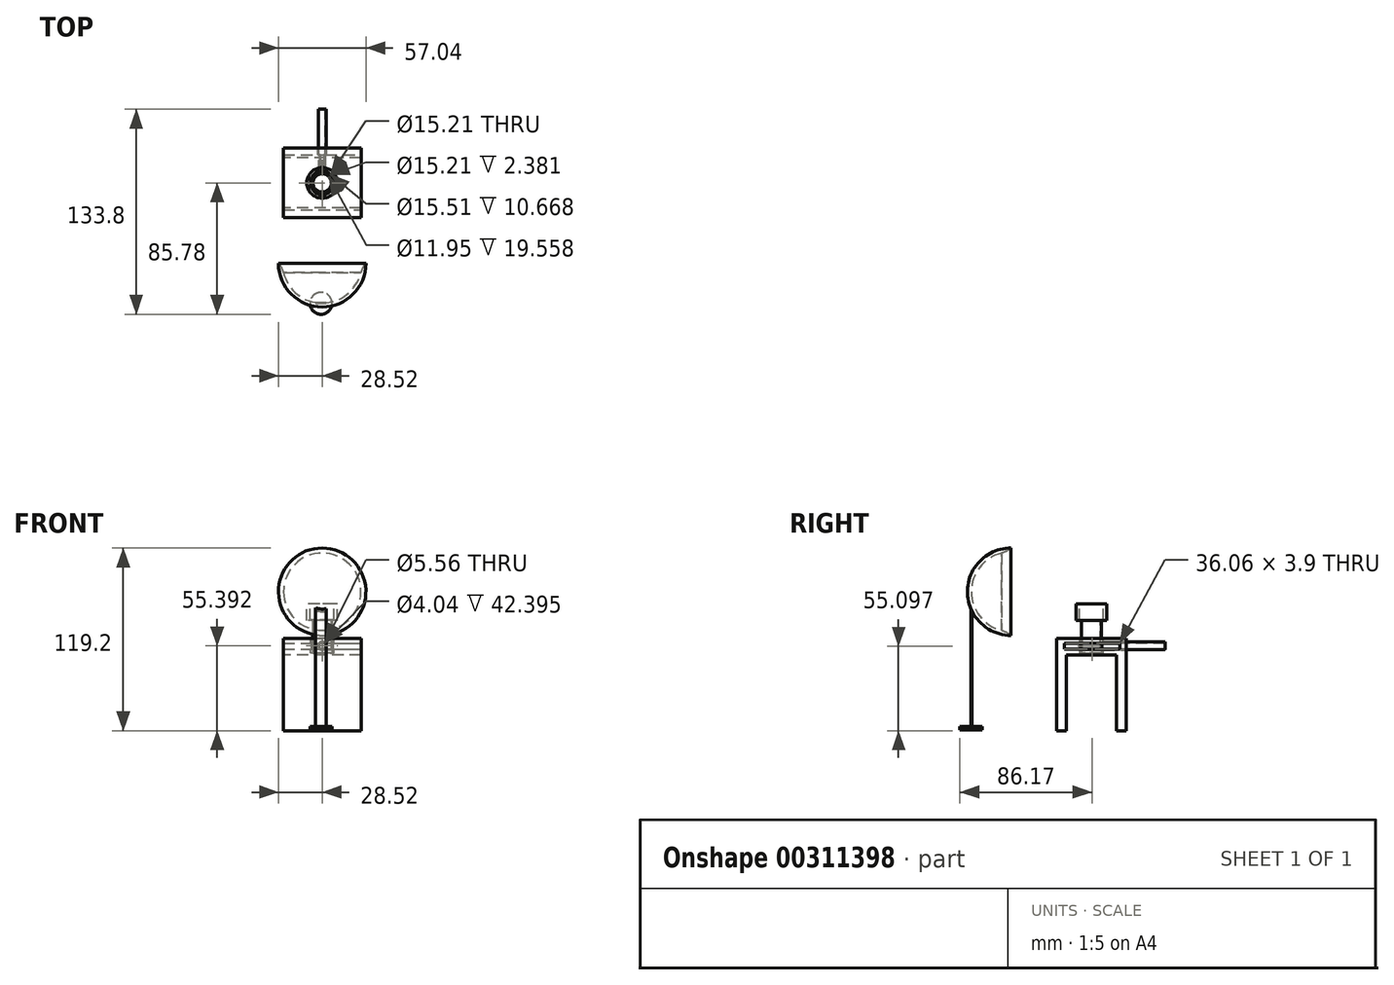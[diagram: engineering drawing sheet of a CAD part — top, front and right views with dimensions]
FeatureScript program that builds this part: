
annotation { "Feature Type Name" : "Feature", "Feature Type Description" : "" }
export const myFeature = defineFeature(function(context is Context, id is Id, definition is map)
    precondition{}
    {
        {
            var Q0;
            Q0=qCreatedBy(makeId("Front.planeOp"),FACE);
            var sketch = newSketch(context, id + "F0", { "sketchPlane" : qUnion([Q0])});
            skLineSegment(sketch, "E0", {"start": v(0, 0) * mm, "end": v(0, 57.05) * mm});
            skCircle(sketch, "E1", {"center": v(0, 28.53) * mm, "radius": 28.52 * mm});
            skSolve(sketch);
        }
        {
            var Q0;
            {var subQ0=sQuery(id+"F0.wireOp",EDGE,"E1");var subQ1=sQuery(id+"F0.wireOp",EDGE,"E0");var subQ2=makeQuery(id+"F0.imprint","INTERSECT",VERTEX,{"disambiguationData":[OD(0.0)],"derivedFrom":[subQ1,subQ0]});Q0=makeQuery(id+"F0.imprint","IMPRINT",FACE,{"disambiguationData":[TD([[makeQuery(id+"F0.imprint","IMPRINT",EDGE,{"disambiguationData":[TD([[subQ2,-1.0]])],"derivedFrom":subQ1}),1.0]])]});}
            var Q1;
            Q1=sQuery(id+"F0.wireOp",EDGE,"E0");
            revolve(context, id + "F1", {"entities" : qUnion([Q0]), "axis" : qUnion([Q1]), "revolveType" : RevolveType.ONE_DIRECTION, "angle" : 180 * degree});
        }
        {
            var Q0;
            Q0=makeQuery(id+"F1.opRevolve","CAP_FACE",FACE,{"disambiguationData":[OSD([sQuery(id+"F0.wireOp",EDGE,"E0"),sQuery(id+"F0.wireOp",EDGE,"E1")])],"isStart":false});
            shell(context, id + "F2", {"entities" : qUnion([Q0]), "thickness" : 2.54 * mm});
        }
        {
            var Q0;
            Q0=makeQuery(id+"F2.opShell","OFFSET_EDGE",EDGE,{"disambiguationData":[OSD([sQuery(id+"F0.wireOp",EDGE,"E1")])]});
            fillet(context, id + "F3", {"entities" : qUnion([Q0]), "radius" : 14.1 * mm, "tangentPropagation" : true, "allowEdgeOverflow" : false});
        }
        {
            var Q0;
            Q0=qCreatedBy(makeId("Front.planeOp"),FACE);
            var sketch = newSketch(context, id + "F4", { "sketchPlane" : qUnion([Q0])});
            skLineSegment(sketch, "E2.bottom", {"start": v(-4.32, 22.58) * mm, "end": v(2.74, 22.58) * mm});
            skLineSegment(sketch, "E2.top", {"start": v(-4.32, 1.52) * mm, "end": v(2.74, 1.52) * mm, "construction": true});
            skLineSegment(sketch, "E2.left", {"start": v(-4.32, 22.58) * mm, "end": v(-4.32, 1.52) * mm});
            skLineSegment(sketch, "E2.right", {"start": v(2.74, 22.58) * mm, "end": v(2.74, 1.52) * mm});
            skLineSegment(sketch, "E3.MirrorCS", {"start": v(-4.32, -19.53) * mm, "end": v(2.74, -19.53) * mm});
            skLineSegment(sketch, "E4.MirrorCS", {"start": v(2.74, -19.53) * mm, "end": v(2.74, 1.52) * mm});
            skLineSegment(sketch, "E5.MirrorCS", {"start": v(-4.32, -19.53) * mm, "end": v(-4.32, 1.52) * mm});
            skLineSegment(sketch, "E6.MirrorCS", {"start": v(2.74, -19.53) * mm, "end": v(2.74, -40.58) * mm});
            skLineSegment(sketch, "E7.MirrorCS", {"start": v(-4.32, -19.53) * mm, "end": v(-4.32, -40.58) * mm});
            skLineSegment(sketch, "E8.MirrorCS", {"start": v(-4.32, -61.63) * mm, "end": v(-4.32, -40.58) * mm});
            skLineSegment(sketch, "E9.MirrorCS", {"start": v(2.74, -61.63) * mm, "end": v(2.74, -40.58) * mm});
            skLineSegment(sketch, "E10.MirrorCS", {"start": v(-4.32, -61.63) * mm, "end": v(2.74, -61.63) * mm});
            skSolve(sketch);
        }
        {
            var Q0;
            Q0 = qSketchRegion(id + "F4", true);
            extrude(context, id + "F5", {"entities" : qUnion([Q0]), "operationType" : NewBodyOperationType.ADD, "depth" : 26.16 * mm, "hasSecondDirection" : true, "secondDirectionOppositeDirection" : false, "secondDirectionDepth" : 25.4 * mm});
        }
        {
            var Q0;
            Q0=makeQuery(id+"F5.opExtrude","SWEPT_FACE",FACE,{"disambiguationData":[OSD([sQuery(id+"F4.wireOp",EDGE,"E10.MirrorCS")])]});
            var sketch = newSketch(context, id + "F6", { "sketchPlane" : qUnion([Q0])});
            skCircle(sketch, "E11", {"center": v(-0.8, 26.16) * mm, "radius": 7.18 * mm});
            skSolve(sketch);
        }
        {
            var Q0;
            Q0 = qSketchRegion(id + "F6", true);
            extrude(context, id + "F7", {"entities" : qUnion([Q0]), "operationType" : NewBodyOperationType.ADD, "oppositeDirection" : true, "depth" : 2.3 * mm});
        }
        {
            var Q0;
            Q0=qCreatedBy(makeId("Right.planeOp"),FACE);
            var sketch = newSketch(context, id + "F8", { "sketchPlane" : qUnion([Q0])});
            skLineSegment(sketch, "E12.bottom", {"start": v(29.82, -1.82) * mm, "end": v(75.06, -1.82) * mm});
            skLineSegment(sketch, "E12.top", {"start": v(29.82, -12.69) * mm, "end": v(75.06, -12.69) * mm});
            skLineSegment(sketch, "E12.left", {"start": v(29.82, -1.82) * mm, "end": v(29.82, -12.69) * mm});
            skLineSegment(sketch, "E12.right", {"start": v(75.06, -1.82) * mm, "end": v(75.06, -12.69) * mm});
            skLineSegment(sketch, "E13.bottom", {"start": v(29.82, -1.82) * mm, "end": v(36.17, -1.82) * mm});
            skLineSegment(sketch, "E13.top", {"start": v(29.82, -62.16) * mm, "end": v(36.17, -62.16) * mm});
            skLineSegment(sketch, "E13.left", {"start": v(29.82, -1.82) * mm, "end": v(29.82, -62.16) * mm});
            skLineSegment(sketch, "E13.right", {"start": v(36.17, -1.82) * mm, "end": v(36.17, -62.16) * mm});
            skPoint(sketch, "E14.oppositeSnap0", {"position": v(75.06, -7.25) * mm});
            skLineSegment(sketch, "E14.bottom", {"start": v(68.7, -1.82) * mm, "end": v(75.06, -1.82) * mm});
            skLineSegment(sketch, "E14.top", {"start": v(68.7, -62.16) * mm, "end": v(75.06, -62.16) * mm});
            skLineSegment(sketch, "E14.left", {"start": v(68.7, -1.82) * mm, "end": v(68.7, -62.16) * mm});
            skLineSegment(sketch, "E14.right", {"start": v(75.06, -1.82) * mm, "end": v(75.06, -62.16) * mm});
            skSolve(sketch);
        }
        {
            var Q0;
            Q0 = qSketchRegion(id + "F8", true);
            extrude(context, id + "F9", {"entities" : qUnion([Q0]), "depth" : 25.4 * mm, "hasSecondDirection" : true, "secondDirectionOppositeDirection" : true, "secondDirectionDepth" : 25.4 * mm});
        }
        {
            var Q0;
            Q0=makeQuery(id+"F9.opExtrude","SWEPT_FACE",FACE,{"disambiguationData":[OSD([sQuery(id+"F8.wireOp",EDGE,"E12.bottom"),sQuery(id+"F8.wireOp",EDGE,"E13.bottom"),sQuery(id+"F8.wireOp",EDGE,"E14.bottom")])]});
            var sketch = newSketch(context, id + "F10", { "sketchPlane" : qUnion([Q0])});
            skCircle(sketch, "E15", {"center": v(0, 52.44) * mm, "radius": 7.6 * mm});
            skPoint(sketch, "E15.centerSnap0", {"position": v(25.4, 52.44) * mm});
            skPoint(sketch, "E15.centerSnap1", {"position": v(0, 29.82) * mm});
            skSolve(sketch);
        }
        {
            var Q0;
            Q0 = qSketchRegion(id + "F10", true);
            extrude(context, id + "F11", {"entities" : qUnion([Q0]), "operationType" : NewBodyOperationType.REMOVE, "oppositeDirection" : true, "depth" : 9.58 * mm});
        }
        {
            var Q0;
            Q0=makeQuery(id+"F9.opExtrude","SWEPT_FACE",FACE,{"disambiguationData":[OSD([sQuery(id+"F8.wireOp",EDGE,"E14.right")])]});
            var sketch = newSketch(context, id + "F12", { "sketchPlane" : qUnion([Q0])});
            skCircle(sketch, "E16", {"center": v(0, -6.77) * mm, "radius": 2.78 * mm});
            skSolve(sketch);
        }
        {
            var Q0;
            Q0 = qSketchRegion(id + "F12", true);
            extrude(context, id + "F13", {"entities" : qUnion([Q0]), "operationType" : NewBodyOperationType.REMOVE, "oppositeDirection" : true, "depth" : 25.4 * mm});
        }
        {
            var Q0;
            Q0=makeQuery(id+"F11.boolean.opBoolean","COPY",FACE,{"derivedFrom":makeQuery(id+"F11.opExtrude","CAP_FACE",FACE,{"disambiguationData":[OSD([sQuery(id+"F10.wireOp",EDGE,"E15")])],"isStart":false})});
            var sketch = newSketch(context, id + "F14", { "sketchPlane" : qUnion([Q0])});
            skCircle(sketch, "E17", {"center": v(0, 52.44) * mm, "radius": 6.43 * mm});
            skSolve(sketch);
        }
        {
            var Q0;
            Q0 = qSketchRegion(id + "F14", true);
            extrude(context, id + "F15", {"entities" : qUnion([Q0]), "depth" : 32 * mm});
        }
        {
            var Q0;
            Q0=makeQuery(id+"F9.opExtrude","SWEPT_FACE",FACE,{"disambiguationData":[OSD([sQuery(id+"F8.wireOp",EDGE,"E14.right")])]});
            var sketch = newSketch(context, id + "F16", { "sketchPlane" : qUnion([Q0])});
            skCircle(sketch, "E18", {"center": v(0, -6.77) * mm, "radius": 2.5 * mm});
            skSolve(sketch);
        }
        {
            var Q0;
            Q0 = qSketchRegion(id + "F16", true);
            extrude(context, id + "F17", {"entities" : qUnion([Q0]), "operationType" : NewBodyOperationType.ADD, "depth" : 25.4 * mm, "hasSecondDirection" : true, "secondDirectionOppositeDirection" : true, "secondDirectionDepth" : 25.4 * mm});
        }
        {
            var Q0;
            Q0=makeQuery(id+"F17.opExtrude","CAP_FACE",FACE,{"disambiguationData":[OSD([sQuery(id+"F16.wireOp",EDGE,"E18")])],"isStart":false});
            shell(context, id + "F18", {"entities" : qUnion([Q0]), "thickness" : 2.54 * mm});
        }
        {
            var Q0;
            Q0=makeQuery(id+"F17.opExtrude","CAP_FACE",FACE,{"disambiguationData":[OSD([sQuery(id+"F16.wireOp",EDGE,"E18")])],"isStart":false});
            var sketch = newSketch(context, id + "F19", { "sketchPlane" : qUnion([Q0])});
            skSolve(sketch);
        }
        {
            var Q0;
            Q0=makeQuery(id+"F19.imprint","IMPRINT",FACE,{"disambiguationData":[TD([[makeQuery(id+"F19.imprint","IMPRINT",EDGE,{"derivedFrom":makeQuery(id+"F17.opExtrude","CAP_EDGE",EDGE,{"disambiguationData":[OSD([sQuery(id+"F16.wireOp",EDGE,"E18")])],"isStart":false})}),1.0]])]});
            var sketch = newSketch(context, id + "F20", { "sketchPlane" : qUnion([Q0])});
            skCircle(sketch, "E19", {"center": v(0, -6.77) * mm, "radius": 2.02 * mm});
            skSolve(sketch);
        }
        {
            var Q0;
            Q0=makeQuery(id+"F9.opExtrude","CAP_FACE",FACE,{"disambiguationData":[OSD([sQuery(id+"F8.wireOp",EDGE,"E12.bottom"),sQuery(id+"F8.wireOp",EDGE,"E12.top"),sQuery(id+"F8.wireOp",EDGE,"E13.bottom"),sQuery(id+"F8.wireOp",EDGE,"E13.top"),sQuery(id+"F8.wireOp",EDGE,"E13.left"),sQuery(id+"F8.wireOp",EDGE,"E13.right"),sQuery(id+"F8.wireOp",EDGE,"E14.bottom"),sQuery(id+"F8.wireOp",EDGE,"E14.top"),sQuery(id+"F8.wireOp",EDGE,"E14.left"),sQuery(id+"F8.wireOp",EDGE,"E14.right")])],"isStart":false});
            var sketch = newSketch(context, id + "F21", { "sketchPlane" : qUnion([Q0])});
            skLineSegment(sketch, "E20.bottom", {"start": v(34.8, -5.11) * mm, "end": v(70.86, -5.11) * mm});
            skLineSegment(sketch, "E20.top", {"start": v(34.8, -9.01) * mm, "end": v(70.86, -9.01) * mm});
            skLineSegment(sketch, "E20.left", {"start": v(34.8, -5.11) * mm, "end": v(34.8, -9.01) * mm});
            skLineSegment(sketch, "E20.right", {"start": v(70.86, -5.11) * mm, "end": v(70.86, -9.01) * mm});
            skSolve(sketch);
        }
        {
            var Q0;
            Q0 = qSketchRegion(id + "F21", true);
            extrude(context, id + "F22", {"entities" : qUnion([Q0]), "operationType" : NewBodyOperationType.REMOVE, "oppositeDirection" : true, "depth" : 75.95 * mm});
        }
        {
            var Q0;
            Q0=makeQuery(id+"F15.opExtrude","CAP_FACE",FACE,{"disambiguationData":[OSD([sQuery(id+"F14.wireOp",EDGE,"E17")])],"isStart":false});
            var sketch = newSketch(context, id + "F23", { "sketchPlane" : qUnion([Q0])});
            skCircle(sketch, "E21", {"center": v(0, 52.44) * mm, "radius": 10 * mm});
            skSolve(sketch);
        }
        {
            var Q0;
            Q0 = qSketchRegion(id + "F23", true);
            extrude(context, id + "F24", {"entities" : qUnion([Q0]), "operationType" : NewBodyOperationType.ADD, "oppositeDirection" : true, "depth" : 10.92 * mm});
        }
        {
            var Q0;
            Q0=makeQuery(id+"F24.boolean.opBoolean","MERGE",FACE,{"derivedFrom":[makeQuery(id+"F15.opExtrude","CAP_FACE",FACE,{"disambiguationData":[OSD([sQuery(id+"F14.wireOp",EDGE,"E17")])],"isStart":false}),makeQuery(id+"F24.opExtrude","CAP_FACE",FACE,{"disambiguationData":[OSD([sQuery(id+"F23.wireOp",EDGE,"E21")])],"isStart":true})]});
            var sketch = newSketch(context, id + "F25", { "sketchPlane" : qUnion([Q0])});
            skCircle(sketch, "E22", {"center": v(0, 52.44) * mm, "radius": 7.75 * mm});
            skSolve(sketch);
        }
        {
            var Q0;
            Q0 = qSketchRegion(id + "F25", true);
            extrude(context, id + "F26", {"entities" : qUnion([Q0]), "operationType" : NewBodyOperationType.REMOVE, "oppositeDirection" : true, "depth" : 10.67 * mm});
        }
        {
            var Q0;
            Q0=makeQuery(id+"F26.boolean.opBoolean","COPY",FACE,{"derivedFrom":makeQuery(id+"F26.opExtrude","CAP_FACE",FACE,{"disambiguationData":[OSD([sQuery(id+"F25.wireOp",EDGE,"E22")])],"isStart":false})});
            var sketch = newSketch(context, id + "F27", { "sketchPlane" : qUnion([Q0])});
            skCircle(sketch, "E23", {"center": v(0, 52.44) * mm, "radius": 5.98 * mm});
            skSolve(sketch);
        }
        {
            var Q0;
            Q0=makeQuery(id+"F22.boolean.opBoolean","COPY",FACE,{"derivedFrom":makeQuery(id+"F22.opExtrude","SWEPT_FACE",FACE,{"disambiguationData":[OSD([sQuery(id+"F21.wireOp",EDGE,"E20.top")])]})});
            var sketch = newSketch(context, id + "F28", { "sketchPlane" : qUnion([Q0])});
            skCircle(sketch, "E24", {"center": v(0, 52.44) * mm, "radius": 7.16 * mm});
            skSolve(sketch);
        }
        {
            var Q0;
            Q0 = qSketchRegion(id + "F28", true);
            extrude(context, id + "F29", {"entities" : qUnion([Q0]), "operationType" : NewBodyOperationType.ADD, "depth" : 7.11 * mm});
        }
        {
            var Q0;
            Q0 = qSketchRegion(id + "F27", true);
            extrude(context, id + "F30", {"entities" : qUnion([Q0]), "operationType" : NewBodyOperationType.REMOVE, "oppositeDirection" : true, "depth" : 19.56 * mm});
        }
        {
            var Q0;
            Q0 = qSketchRegion(id + "F20", true);
            extrude(context, id + "F31", {"entities" : qUnion([Q0]), "operationType" : NewBodyOperationType.REMOVE, "oppositeDirection" : true, "depth" : 46.66 * mm});
        }
    });
